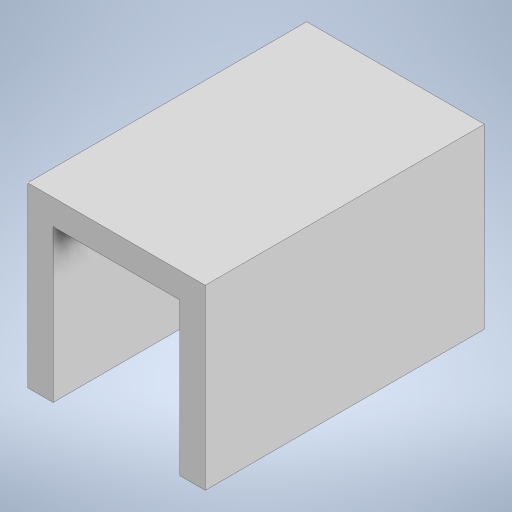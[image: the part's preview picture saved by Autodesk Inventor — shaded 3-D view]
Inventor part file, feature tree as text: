
AUTODESK INVENTOR PART (.ipt)
format: ipt  version: 2023 (Build 270158000, 158)  size: 192,512 bytes
history: native  units: in
note: dims shown in document units (in); Inventor stores cm internally (conversion verified against a paired STEP export)
features: sketch x9, extrude x4
ambient origin geometry x8: Origin, YZ Plane, XZ Plane, XY Plane, X Axis, Y Axis, Z Axis, Center Point
bodies: Solid1 (feature_tree)
feature tree (13):
  extrude  "Extrusion1"  Depth=0.5512in
  extrude  "Extrusion2"  Depth=0.3937in
  sketch  "Sketch8"  dims[d5=0.7874in d6=0.7874in d7=0.0in]
  sketch  "Sketch9"  dims[d30=0.1969in d31=0.4724in]
  sketch  "Sketch11"  dims[d32=0.0787in d33=0.0in]
  sketch  "Sketch14"  dims[d34=0.1772in]
  sketch  "Sketch15"  dims[d35=0.1772in]
  extrude  "Extrusion10"  Depth=0.7874in TaperAngle=0.0deg
  extrude  "Extrusion11"  Depth=0.4724in
  sketch  "Sketch1"  dims[d0=0.5512in d1=0.5512in]
  sketch  "Sketch2"  dims[d2=0.8661in d3=0.0in d4=0.3937in]
  sketch  "Sketch16"  dims[d36=0.3543in d37=0.0in]
  sketch  "Sketch17"
